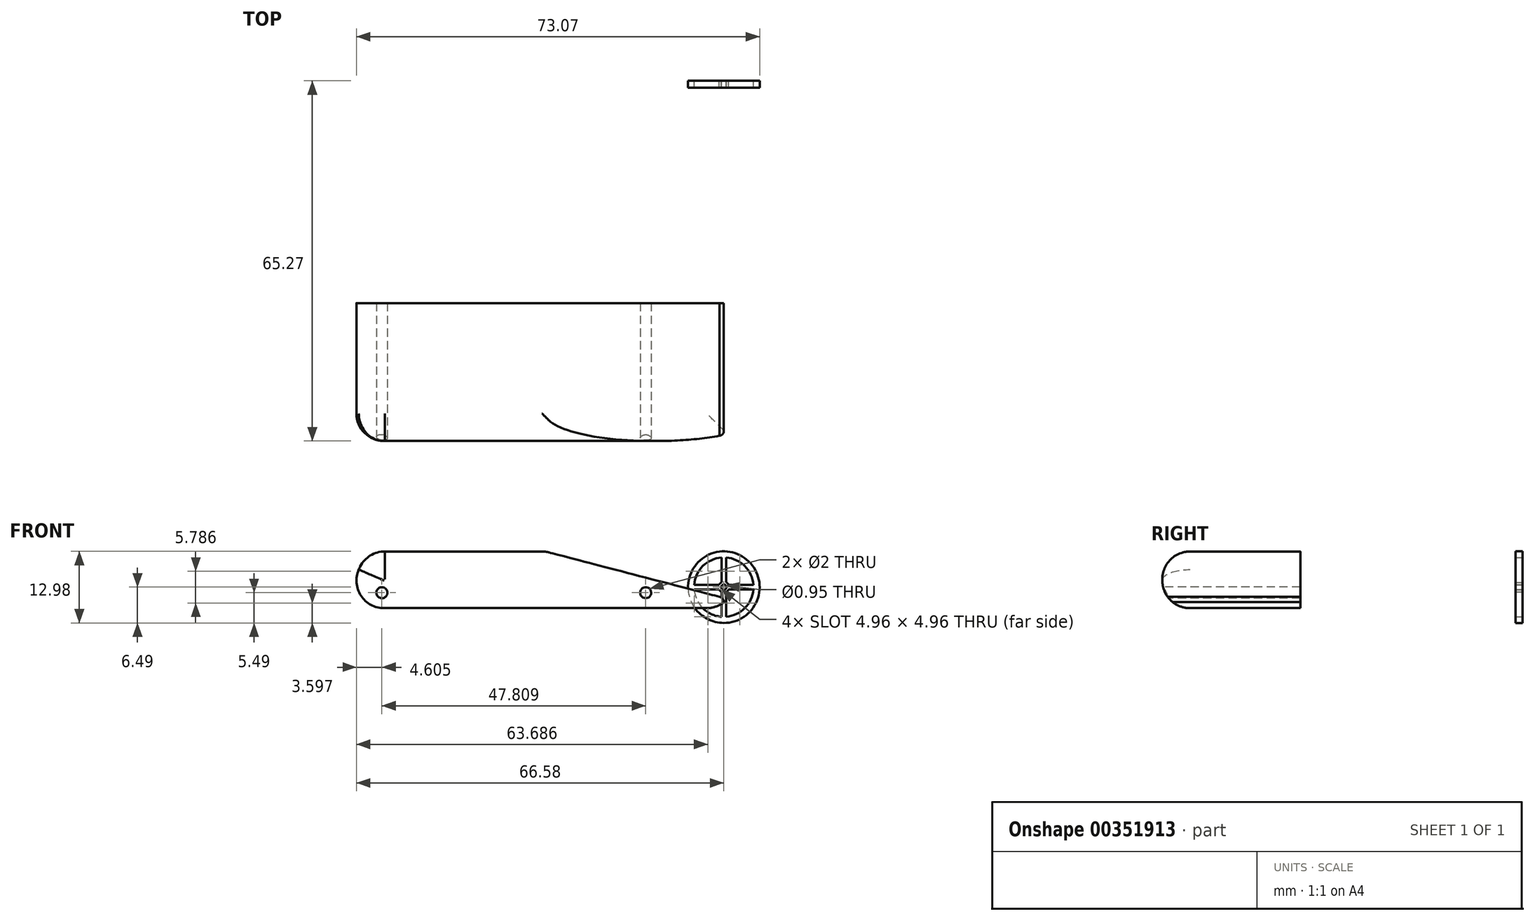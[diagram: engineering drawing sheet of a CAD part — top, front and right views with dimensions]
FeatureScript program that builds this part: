
annotation { "Feature Type Name" : "Feature", "Feature Type Description" : "" }
export const myFeature = defineFeature(function(context is Context, id is Id, definition is map)
    precondition{}
    {
        {
            var Q0;
            Q0=qCreatedBy(makeId("Front.planeOp"),FACE);
            var sketch = newSketch(context, id + "F0", { "sketchPlane" : qUnion([Q0])});
            skCircle(sketch, "E0", {"center": v(0, 0) * mm, "radius": 6.49 * mm});
            skArc(sketch, "E1", {"start": v(-5.37, -0.41) * mm, "mid": v(-3.8, -3.8) * mm, "end": v(-0.42, -5.37) * mm});
            skLineSegment(sketch, "E2.bottom", {"start": v(5.37, 0.41) * mm, "end": v(0.86, 0.41) * mm});
            skLineSegment(sketch, "E2.top", {"start": v(5.37, -0.41) * mm, "end": v(0.86, -0.41) * mm});
            skLineSegment(sketch, "E3.left", {"start": v(0.34, 5.38) * mm, "end": v(0.34, 5.37) * mm});
            skLineSegment(sketch, "E3.right", {"start": v(-0.34, 5.38) * mm, "end": v(-0.34, 5.37) * mm});
            skArc(sketch, "E4", {"start": v(-0.86, -0.41) * mm, "mid": v(-0.68, -0.68) * mm, "end": v(-0.42, -0.86) * mm});
            skLineSegment(sketch, "E5.trimOffspring", {"start": v(-0.34, -5.37) * mm, "end": v(-0.34, -5.38) * mm});
            skLineSegment(sketch, "E6.trimOffspring", {"start": v(-0.86, 0.41) * mm, "end": v(-5.37, 0.41) * mm});
            skLineSegment(sketch, "E7.trimOffspring", {"start": v(0.34, -5.37) * mm, "end": v(0.34, -5.38) * mm});
            skLineSegment(sketch, "E8.trimOffspring", {"start": v(-0.86, -0.41) * mm, "end": v(-5.37, -0.41) * mm});
            skArc(sketch, "E9.trimOffspring", {"start": v(-0.42, 0.86) * mm, "mid": v(-0.68, 0.68) * mm, "end": v(-0.86, 0.41) * mm});
            skArc(sketch, "E10.trimOffspring", {"start": v(0.86, 0.41) * mm, "mid": v(0.68, 0.68) * mm, "end": v(0.42, 0.86) * mm});
            skArc(sketch, "E11.trimOffspring", {"start": v(0.42, -0.86) * mm, "mid": v(0.68, -0.68) * mm, "end": v(0.86, -0.41) * mm});
            skCircle(sketch, "E12", {"center": v(0, 0) * mm, "radius": 0.47 * mm});
            skArc(sketch, "E13.trimOffspring", {"start": v(-0.42, 5.37) * mm, "mid": v(-3.8, 3.8) * mm, "end": v(-5.37, 0.41) * mm});
            skArc(sketch, "E14.trimOffspring", {"start": v(5.37, 0.41) * mm, "mid": v(3.8, 3.8) * mm, "end": v(0.42, 5.37) * mm});
            skArc(sketch, "E15.trimOffspring", {"start": v(0.42, -5.37) * mm, "mid": v(3.8, -3.8) * mm, "end": v(5.37, -0.41) * mm});
            skLineSegment(sketch, "E16.right", {"start": v(-0.42, 5.37) * mm, "end": v(-0.42, 0.86) * mm});
            skLineSegment(sketch, "E17.trimOffspring", {"start": v(-0.42, -0.86) * mm, "end": v(-0.42, -5.37) * mm});
            skLineSegment(sketch, "E18.trimOffspring", {"start": v(0.42, -0.86) * mm, "end": v(0.42, -5.37) * mm});
            skLineSegment(sketch, "E19", {"start": v(0.42, 0.86) * mm, "end": v(0.42, 5.37) * mm});
            skSolve(sketch);
        }
        {
            var Q0;
            Q0=qSketchRegion(id+"F0",true);
            extrude(context, id + "F1", {"entities" : qUnion([Q0]), "depth" : 1.27 * mm});
        }
        {
            var Q0;
            Q0=qCreatedBy(makeId("Right.planeOp"),FACE);
            var sketch = newSketch(context, id + "F2", { "sketchPlane" : qUnion([Q0])});
            skLineSegment(sketch, "E20", {"start": v(0, 0) * mm, "end": v(0, -3.81) * mm});
            skLineSegment(sketch, "E21.left", {"start": v(-1.27, -3.81) * mm, "end": v(-1.27, 3.8) * mm});
            skLineSegment(sketch, "E22", {"start": v(-1.27, -3.81) * mm, "end": v(-40.27, -3.81) * mm});
            skLineSegment(sketch, "E23", {"start": v(-1.27, 3.8) * mm, "end": v(-40.27, 3.8) * mm});
            skLineSegment(sketch, "E24", {"start": v(-40.27, 3.8) * mm, "end": v(-40.27, -3.81) * mm});
            skLineSegment(sketch, "E25", {"start": v(-1.27, 0) * mm, "end": v(-40.27, 0) * mm});
            skLineSegment(sketch, "E26", {"start": v(-40.27, -3.81) * mm, "end": v(-40.27, 11.19) * mm});
            skLineSegment(sketch, "E27", {"start": v(-40.27, 11.19) * mm, "end": v(-1.27, 11.2) * mm});
            skLineSegment(sketch, "E28", {"start": v(-1.27, 11.2) * mm, "end": v(-1.27, 3.8) * mm});
            skSolve(sketch);
        }
        {
            var Q0;
            Q0 = qSketchRegion(id + "F2", true);
            extrude(context, id + "F3", {"entities" : qUnion([Q0]), "operationType" : NewBodyOperationType.ADD, "oppositeDirection" : true, "depth" : 67 * mm});
        }
        {
            var Q0;
            Q0=makeQuery(id+"F3.opExtrude","SWEPT_FACE",FACE,{"disambiguationData":[OSD([sQuery(id+"F2.wireOp",EDGE,"E26")])]});
            var sketch = newSketch(context, id + "F4", { "sketchPlane" : qUnion([Q0])});
            skLineSegment(sketch, "E29", {"start": v(-67, 11.19) * mm, "end": v(-67, 9.19) * mm});
            skLineSegment(sketch, "E30", {"start": v(-67, -0.81) * mm, "end": v(-67, -3.8) * mm});
            skLineSegment(sketch, "E31", {"start": v(-67, -3.81) * mm, "end": v(-14.6, -3.81) * mm});
            skLineSegment(sketch, "E32", {"start": v(-65.5, -3.81) * mm, "end": v(-67, -2.31) * mm});
            skLineSegment(sketch, "E33", {"start": v(-14.6, -3.81) * mm, "end": v(0, -3.81) * mm});
            skLineSegment(sketch, "E34", {"start": v(0, -3.81) * mm, "end": v(0, -2.72) * mm});
            skPoint(sketch, "E35.orphan", {"position": v(0, 0) * mm});
            skPoint(sketch, "E36.visualSharp", {"position": v(-67, 9.19) * mm});
            skArc(sketch, "E36.filletArc", {"start": v(-63.87, 6.46) * mm, "mid": v(-66.18, 3.15) * mm, "end": v(-67, -0.8) * mm});
            skPoint(sketch, "E37.visualSharp", {"position": v(-37, 9.19) * mm});
            skPoint(sketch, "E38.endSnap0", {"position": v(0, -2.86) * mm});
            skPoint(sketch, "E39.visualSharp", {"position": v(-27.59, 3.69) * mm});
            skPoint(sketch, "E40.visualSharp", {"position": v(0, -1.9) * mm});
            skArc(sketch, "E40.filletArc", {"start": v(0, -2.72) * mm, "mid": v(-0.23, -2.09) * mm, "end": v(-0.8, -1.74) * mm});
            skLineSegment(sketch, "E41", {"start": v(-32.33, 6.46) * mm, "end": v(-0.8, -1.74) * mm});
            skLineSegment(sketch, "E42", {"start": v(-32.33, 6.46) * mm, "end": v(-63.87, 6.46) * mm});
            skSolve(sketch);
        }
        {
            var Q0;
            Q0 = qSketchRegion(id + "F4", true);
            extrude(context, id + "F5", {"entities" : qUnion([Q0]), "operationType" : NewBodyOperationType.ADD, "depth" : 25 * mm});
        }
        {
            var Q0;
            Q0=makeQuery(id+"F5.boolean.opBoolean","MERGE",FACE,{"derivedFrom":[makeQuery(id+"F3.opExtrude","CAP_FACE",FACE,{"disambiguationData":[OSD([sQuery(id+"F2.wireOp",EDGE,"E21.left"),sQuery(id+"F2.wireOp",EDGE,"E22"),sQuery(id+"F2.wireOp",EDGE,"E26"),sQuery(id+"F2.wireOp",EDGE,"E27"),sQuery(id+"F2.wireOp",EDGE,"E28")])],"isStart":true}),makeQuery(id+"F5.opExtrude","SWEPT_FACE",FACE,{"disambiguationData":[OSD([sQuery(id+"F4.wireOp",EDGE,"E34")])]})]});
            var sketch = newSketch(context, id + "F6", { "sketchPlane" : qUnion([Q0])});
            skLineSegment(sketch, "E43.bottom", {"start": v(-1.27, -3.81) * mm, "end": v(-40.27, -3.81) * mm});
            skLineSegment(sketch, "E43.top", {"start": v(-1.27, 11.19) * mm, "end": v(-40.27, 11.19) * mm});
            skLineSegment(sketch, "E43.left", {"start": v(-1.27, -3.81) * mm, "end": v(-1.27, 11.19) * mm});
            skLineSegment(sketch, "E43.right", {"start": v(-40.27, -3.81) * mm, "end": v(-40.27, 11.19) * mm});
            skSolve(sketch);
        }
        {
            var Q0;
            Q0 = qSketchRegion(id + "F6", true);
            extrude(context, id + "F7", {"entities" : qUnion([Q0]), "operationType" : NewBodyOperationType.REMOVE, "oppositeDirection" : true, "depth" : 100 * mm});
        }
        {
            var Q0;
            Q0=makeQuery(id+"F5.opExtrude","CAP_EDGE",EDGE,{"disambiguationData":[OSD([sQuery(id+"F4.wireOp",EDGE,"E42")])],"isStart":true});
            var Q1;
            Q1=makeQuery(id+"F5.opExtrude","SWEPT_EDGE",EDGE,{"disambiguationData":[OSD([sQuery(id+"F4.wireOp",EDGE,"E41"),sQuery(id+"F4.wireOp",EDGE,"E42")])]});
            var Q2;
            Q2=makeQuery(id+"F5.opExtrude","CAP_EDGE",EDGE,{"disambiguationData":[OSD([sQuery(id+"F4.wireOp",EDGE,"E42")])],"isStart":false});
            fillet(context, id + "F8", {"entities" : qUnion([Q0, Q1, Q2]), "radius" : 5 * mm, "tangentPropagation" : true, "allowEdgeOverflow" : false});
        }
        {
            var Q0;
            Q0=makeQuery(id+"F8.opFillet","BLEND_EDGE",EDGE,{"blendedFrom":[makeQuery(id+"F5.opExtrude","CAP_EDGE",EDGE,{"disambiguationData":[OSD([sQuery(id+"F4.wireOp",EDGE,"E42")])],"isStart":false}),makeQuery(id+"F5.opExtrude","SWEPT_FACE",FACE,{"disambiguationData":[OSD([sQuery(id+"F4.wireOp",EDGE,"E36.filletArc")])]})],"blendedInto":[makeQuery(id+"F5.opExtrude","SWEPT_FACE",FACE,{"disambiguationData":[OSD([sQuery(id+"F4.wireOp",EDGE,"E36.filletArc")])]})]});
            fillet(context, id + "F9", {"entities" : qUnion([Q0]), "radius" : 5 * mm, "tangentPropagation" : true, "allowEdgeOverflow" : false});
        }
        {
            var Q0;
            Q0=makeQuery(id+"F5.boolean.opBoolean","MERGE",EDGE,{"derivedFrom":[makeQuery(id+"F3.opExtrude","CAP_EDGE",EDGE,{"disambiguationData":[OSD([sQuery(id+"F2.wireOp",EDGE,"E22")])],"isStart":true}),makeQuery(id+"F5.opExtrude","SWEPT_EDGE",EDGE,{"disambiguationData":[OSD([sQuery(id+"F4.wireOp",EDGE,"E33"),sQuery(id+"F4.wireOp",EDGE,"E34")])]})]});
            var Q1;
            Q1=makeQuery(id+"F5.opExtrude","CAP_EDGE",EDGE,{"disambiguationData":[OSD([sQuery(id+"F4.wireOp",EDGE,"E31"),sQuery(id+"F4.wireOp",EDGE,"E33")])],"isStart":false});
            fillet(context, id + "F10", {"entities" : qUnion([Q0, Q1]), "radius" : 5 * mm, "tangentPropagation" : true, "allowEdgeOverflow" : false});
        }
        {
            var Q0;
            Q0=makeQuery(id+"F5.opExtrude","CAP_FACE",FACE,{"disambiguationData":[OSD([sQuery(id+"F4.wireOp",EDGE,"E30"),sQuery(id+"F4.wireOp",EDGE,"E31"),sQuery(id+"F4.wireOp",EDGE,"E33"),sQuery(id+"F4.wireOp",EDGE,"E34"),sQuery(id+"F4.wireOp",EDGE,"E36.filletArc"),sQuery(id+"F4.wireOp",EDGE,"E40.filletArc"),sQuery(id+"F4.wireOp",EDGE,"E41"),sQuery(id+"F4.wireOp",EDGE,"E42")])],"isStart":false});
            var sketch = newSketch(context, id + "F11", { "sketchPlane" : qUnion([Q0])});
            skCircle(sketch, "E44", {"center": v(-61.98, -1) * mm, "radius": 1 * mm});
            skCircle(sketch, "E45", {"center": v(-14.17, -1) * mm, "radius": 1 * mm});
            skSolve(sketch);
        }
        {
            var Q0;
            Q0=makeQuery(id+"F11.imprint","IMPRINT",FACE,{"disambiguationData":[TD([[makeQuery(id+"F11.imprint","IMPRINT",EDGE,{"derivedFrom":sQuery(id+"F11.wireOp",EDGE,"E44")}),1.0]])]});
            var Q1;
            Q1=makeQuery(id+"F11.imprint","IMPRINT",FACE,{"disambiguationData":[TD([[makeQuery(id+"F11.imprint","IMPRINT",EDGE,{"derivedFrom":sQuery(id+"F11.wireOp",EDGE,"E45")}),1.0]])]});
            extrude(context, id + "F12", {"entities" : qUnion([Q0, Q1]), "operationType" : NewBodyOperationType.REMOVE, "oppositeDirection" : true, "depth" : 100 * mm});
        }
    });
